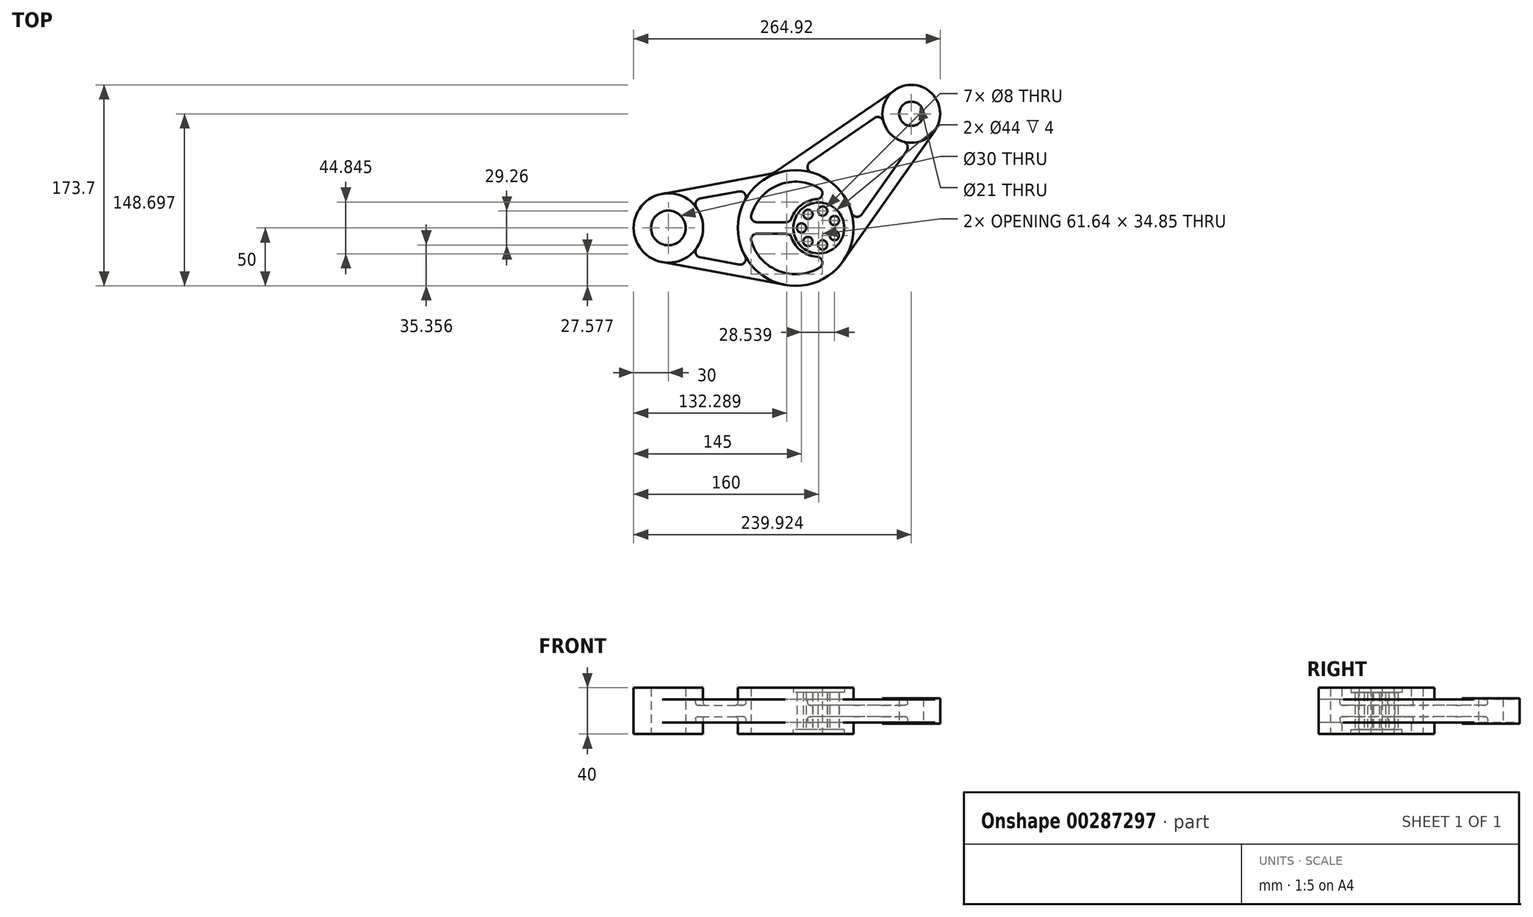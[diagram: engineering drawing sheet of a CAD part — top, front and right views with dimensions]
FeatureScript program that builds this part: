
annotation { "Feature Type Name" : "Feature", "Feature Type Description" : "" }
export const myFeature = defineFeature(function(context is Context, id is Id, definition is map)
    precondition{}
    {
        {
            var Q0;
            Q0=qCreatedBy(makeId("Top.planeOp"),FACE);
            var sketch = newSketch(context, id + "F0", { "sketchPlane" : qUnion([Q0])});
            skLineSegment(sketch, "E0", {"start": v(0, 0) * mm, "end": v(-130, 0) * mm, "construction": true});
            skLineSegment(sketch, "E1", {"start": v(0, 0) * mm, "end": v(79.92, 98.7) * mm, "construction": true});
            skCircle(sketch, "E2", {"center": v(-130, 0) * mm, "radius": 15 * mm});
            skCircle(sketch, "E3", {"center": v(-130, 0) * mm, "radius": 30 * mm});
            skCircle(sketch, "E4", {"center": v(79.92, 98.7) * mm, "radius": 10.5 * mm});
            skCircle(sketch, "E5", {"center": v(79.92, 98.7) * mm, "radius": 25 * mm});
            skCircle(sketch, "E6", {"center": v(-20, 0) * mm, "radius": 50 * mm});
            skArc(sketch, "E7", {"start": v(-58.33, -11.43) * mm, "mid": v(-34.4, -37.32) * mm, "end": v(0.71, -34.22) * mm});
            skArc(sketch, "E8", {"start": v(-23.57, -8.33) * mm, "mid": v(-15.06, -19.95) * mm, "end": v(-1.56, -24.95) * mm});
            skCircle(sketch, "E9", {"center": v(0, 0) * mm, "radius": 22 * mm});
            skCircle(sketch, "E10", {"center": v(0, 0) * mm, "radius": 15 * mm, "construction": true});
            skCircle(sketch, "E11", {"center": v(-15, 0) * mm, "radius": 4 * mm});
            skCircle(sketch, "E12.1.0", {"center": v(-9.34, 11.74) * mm, "radius": 4 * mm});
            skCircle(sketch, "E12.2.0", {"center": v(3.37, 14.62) * mm, "radius": 4 * mm});
            skCircle(sketch, "E12.3.0", {"center": v(13.54, 6.46) * mm, "radius": 4 * mm});
            skCircle(sketch, "E12.4.0", {"center": v(13.48, -6.58) * mm, "radius": 4 * mm});
            skCircle(sketch, "E12.5.0", {"center": v(3.25, -14.64) * mm, "radius": 4 * mm});
            skCircle(sketch, "E12.6.0", {"center": v(-9.44, -11.66) * mm, "radius": 4 * mm});
            skLineSegment(sketch, "E12.anchor1", {"start": v(0, 0) * mm, "end": v(-15, 0) * mm, "construction": true});
            skLineSegment(sketch, "E12.anchor2", {"start": v(0, 0) * mm, "end": v(-9.44, -11.66) * mm, "construction": true});
            skLineSegment(sketch, "E13", {"start": v(-135.45, -29.5) * mm, "end": v(-29.1, -49.17) * mm});
            skLineSegment(sketch, "E14", {"start": v(-135.45, 29.5) * mm, "end": v(-42, 46.78) * mm});
            skLineSegment(sketch, "E15", {"start": v(65.8, 119.33) * mm, "end": v(-37.4, 48.68) * mm});
            skLineSegment(sketch, "E16", {"start": v(100.38, 84.32) * mm, "end": v(20.9, -28.75) * mm});
            skLineSegment(sketch, "E17", {"start": v(-53.54, -5) * mm, "end": v(-28.28, -5) * mm});
            skLineSegment(sketch, "E18", {"start": v(-53.54, 5) * mm, "end": v(-28.28, 5) * mm});
            skArc(sketch, "E19.trimOffspring", {"start": v(0.71, 34.22) * mm, "mid": v(-34.4, 37.32) * mm, "end": v(-58.33, 11.43) * mm});
            skArc(sketch, "E20.trimOffspring", {"start": v(-1.56, 24.95) * mm, "mid": v(-15.06, 19.95) * mm, "end": v(-23.57, 8.33) * mm});
            skPoint(sketch, "E21.visualSharp", {"position": v(-59.69, 5) * mm});
            skArc(sketch, "E21.filletArc", {"start": v(-58.33, 11.43) * mm, "mid": v(-57.55, 7.01) * mm, "end": v(-53.54, 5) * mm});
            skPoint(sketch, "E22.visualSharp", {"position": v(-59.69, -5) * mm});
            skArc(sketch, "E22.filletArc", {"start": v(-53.54, -5) * mm, "mid": v(-57.55, -7.01) * mm, "end": v(-58.33, -11.43) * mm});
            skPoint(sketch, "E23.visualSharp", {"position": v(-24.5, 5) * mm});
            skArc(sketch, "E23.filletArc", {"start": v(-28.28, 5) * mm, "mid": v(-25.4, 5.92) * mm, "end": v(-23.57, 8.33) * mm});
            skPoint(sketch, "E24.visualSharp", {"position": v(-24.5, -5) * mm});
            skArc(sketch, "E24.filletArc", {"start": v(-23.57, -8.33) * mm, "mid": v(-25.4, -5.92) * mm, "end": v(-28.28, -5) * mm});
            skArc(sketch, "E25", {"start": v(0.71, -34.22) * mm, "mid": v(2.98, -28.75) * mm, "end": v(-1.56, -24.95) * mm});
            skArc(sketch, "E26", {"start": v(-1.56, 24.95) * mm, "mid": v(2.98, 28.75) * mm, "end": v(0.71, 34.22) * mm});
            skArc(sketch, "E27.filletArc", {"start": v(-42, 46.78) * mm, "mid": v(-39.6, 47.49) * mm, "end": v(-37.4, 48.68) * mm});
            skSolve(sketch);
        }
        {
            var Q0;
            Q0=makeQuery(id+"F0.imprint","IMPRINT",FACE,{"disambiguationData":[TD([[makeQuery(id+"F0.imprint","IMPRINT",EDGE,{"derivedFrom":sQuery(id+"F0.wireOp",EDGE,"E2")}),-1.0]])]});
            extrude(context, id + "F1", {"entities" : qUnion([Q0]), "depth" : 20 * mm});
        }
        {
            var Q0;
            Q0=makeQuery(id+"F0.imprint","IMPRINT",FACE,{"disambiguationData":[TD([[makeQuery(id+"F0.imprint","IMPRINT",EDGE,{"derivedFrom":sQuery(id+"F0.wireOp",EDGE,"E7")}),-1.0]])]});
            extrude(context, id + "F2", {"entities" : qUnion([Q0]), "depth" : 20 * mm});
        }
        {
            var Q0;
            Q0=makeQuery(id+"F0.imprint","IMPRINT",FACE,{"disambiguationData":[TD([[makeQuery(id+"F0.imprint","IMPRINT",EDGE,{"derivedFrom":sQuery(id+"F0.wireOp",EDGE,"E9")}),1.0]])]});
            extrude(context, id + "F3", {"entities" : qUnion([Q0]), "operationType" : NewBodyOperationType.ADD, "depth" : 16 * mm});
        }
        {
            var Q0;
            Q0=makeQuery(id+"F0.imprint","IMPRINT",FACE,{"disambiguationData":[TD([[makeQuery(id+"F0.imprint","IMPRINT",EDGE,{"derivedFrom":sQuery(id+"F0.wireOp",EDGE,"E4")}),-1.0]])]});
            extrude(context, id + "F4", {"entities" : qUnion([Q0]), "depth" : 11 * mm});
        }
        {
            var Q0;
            {var subQ0=sQuery(id+"F0.wireOp",EDGE,"E13");Q0=makeQuery(id+"F0.imprint","IMPRINT",FACE,{"disambiguationData":[TD([[makeQuery(id+"F0.imprint","IMPRINT",EDGE,{"derivedFrom":subQ0}),1.0]])]});}
            extrude(context, id + "F5", {"entities" : qUnion([Q0]), "operationType" : NewBodyOperationType.ADD, "depth" : 10 * mm});
        }
        {
            var Q0;
            Q0=makeQuery(id+"F5.opExtrude","CAP_FACE",FACE,{"disambiguationData":[OSD([sQuery(id+"F0.wireOp",EDGE,"E3"),sQuery(id+"F0.wireOp",EDGE,"E5"),sQuery(id+"F0.wireOp",EDGE,"E6"),sQuery(id+"F0.wireOp",EDGE,"E13"),sQuery(id+"F0.wireOp",EDGE,"E14"),sQuery(id+"F0.wireOp",EDGE,"E15"),sQuery(id+"F0.wireOp",EDGE,"E16"),sQuery(id+"F0.wireOp",EDGE,"E27.filletArc")])],"isStart":false});
            var sketch = newSketch(context, id + "F6", { "sketchPlane" : qUnion([Q0])});
            skArc(sketch, "E28.0", {"start": v(-105.68, -17.57) * mm, "mid": v(-100, 0) * mm, "end": v(-105.68, 17.57) * mm});
            skArc(sketch, "E29.0", {"start": v(-63.71, 24.28) * mm, "mid": v(-70, 0) * mm, "end": v(-63.71, -24.28) * mm});
            skLineSegment(sketch, "E30.0", {"start": v(-135.45, 29.5) * mm, "end": v(-42, 46.78) * mm, "construction": true});
            skLineSegment(sketch, "E31.0", {"start": v(-135.45, -29.5) * mm, "end": v(-29.1, -49.17) * mm, "construction": true});
            skLineSegment(sketch, "E32.0", {"start": v(65.8, 119.33) * mm, "end": v(-37.4, 48.68) * mm, "construction": true});
            skLineSegment(sketch, "E33.0", {"start": v(100.38, 84.32) * mm, "end": v(20.9, -28.75) * mm, "construction": true});
            skArc(sketch, "E34.0", {"start": v(55.77, 92.26) * mm, "mid": v(62.14, 81.13) * mm, "end": v(73.19, 74.62) * mm});
            skLineSegment(sketch, "E35.0", {"start": v(-102.54, 25.42) * mm, "end": v(-69, 31.62) * mm});
            skLineSegment(sketch, "E36.0", {"start": v(-102.54, -25.42) * mm, "end": v(-69, -31.62) * mm});
            skLineSegment(sketch, "E37.0", {"start": v(48.11, 95.1) * mm, "end": v(-7.59, 56.97) * mm});
            skLineSegment(sketch, "E38.0", {"start": v(75.93, 66.93) * mm, "end": v(37.12, 11.71) * mm});
            skArc(sketch, "E39.trimOffspring", {"start": v(-135.45, 29.5) * mm, "mid": v(-160, 0) * mm, "end": v(-135.45, -29.5) * mm, "construction": true});
            skArc(sketch, "E40.trimOffspring", {"start": v(28.2, 13.26) * mm, "mid": v(15.57, 35.14) * mm, "end": v(-6.15, 48.04) * mm});
            skArc(sketch, "E41.trimOffspring", {"start": v(-29.1, -49.17) * mm, "mid": v(-1.1, -46.29) * mm, "end": v(20.9, -28.75) * mm, "construction": true});
            skPoint(sketch, "E42.visualSharp", {"position": v(-111.65, 23.73) * mm});
            skArc(sketch, "E42.filletArc", {"start": v(-102.54, 25.42) * mm, "mid": v(-106.27, 22.36) * mm, "end": v(-105.68, 17.57) * mm});
            skPoint(sketch, "E43.visualSharp", {"position": v(-111.65, -23.73) * mm});
            skArc(sketch, "E43.filletArc", {"start": v(-105.68, -17.57) * mm, "mid": v(-106.27, -22.36) * mm, "end": v(-102.54, -25.42) * mm});
            skPoint(sketch, "E44.visualSharp", {"position": v(54.95, 99.78) * mm});
            skArc(sketch, "E44.filletArc", {"start": v(55.77, 92.26) * mm, "mid": v(52.67, 95.66) * mm, "end": v(48.11, 95.1) * mm});
            skPoint(sketch, "E45.visualSharp", {"position": v(80.7, 73.7) * mm});
            skArc(sketch, "E45.filletArc", {"start": v(75.93, 66.93) * mm, "mid": v(76.55, 71.49) * mm, "end": v(73.19, 74.62) * mm});
            skArc(sketch, "E46", {"start": v(-63.71, 24.28) * mm, "mid": v(-64.02, 29.62) * mm, "end": v(-69, 31.62) * mm});
            skArc(sketch, "E47", {"start": v(-69, -31.62) * mm, "mid": v(-64.02, -29.62) * mm, "end": v(-63.71, -24.28) * mm});
            skArc(sketch, "E48", {"start": v(-7.59, 56.97) * mm, "mid": v(-9.7, 52.05) * mm, "end": v(-6.15, 48.04) * mm});
            skArc(sketch, "E49", {"start": v(28.2, 13.26) * mm, "mid": v(32.17, 9.66) * mm, "end": v(37.12, 11.71) * mm});
            skSolve(sketch);
        }
        {
            var Q0;
            Q0=makeQuery(id+"F6.imprint","IMPRINT",FACE,{"disambiguationData":[TD([[makeQuery(id+"F6.imprint","IMPRINT",EDGE,{"derivedFrom":sQuery(id+"F6.wireOp",EDGE,"E28.0")}),-1.0]])]});
            var Q1;
            Q1=makeQuery(id+"F6.imprint","IMPRINT",FACE,{"disambiguationData":[TD([[makeQuery(id+"F6.imprint","IMPRINT",EDGE,{"derivedFrom":sQuery(id+"F6.wireOp",EDGE,"E34.0")}),-1.0]])]});
            extrude(context, id + "F7", {"entities" : qUnion([Q0, Q1]), "operationType" : NewBodyOperationType.REMOVE, "oppositeDirection" : true, "depth" : 5 * mm});
        }
        {
            var Q0;
            Q0=makeQuery(id+"F7.boolean.opBoolean","COPY",EDGE,{"derivedFrom":makeQuery(id+"F7.opExtrude","CAP_EDGE",EDGE,{"disambiguationData":[OSD([sQuery(id+"F6.wireOp",EDGE,"E35.0")])],"isStart":false})});
            var Q1;
            Q1=makeQuery(id+"F7.boolean.opBoolean","COPY",EDGE,{"derivedFrom":makeQuery(id+"F7.opExtrude","CAP_EDGE",EDGE,{"disambiguationData":[OSD([sQuery(id+"F6.wireOp",EDGE,"E28.0")])],"isStart":false})});
            var Q2;
            Q2=makeQuery(id+"F7.boolean.opBoolean","COPY",EDGE,{"derivedFrom":makeQuery(id+"F7.opExtrude","CAP_EDGE",EDGE,{"disambiguationData":[OSD([sQuery(id+"F6.wireOp",EDGE,"E37.0")])],"isStart":false})});
            var Q3;
            Q3=makeQuery(id+"F7.boolean.opBoolean","COPY",EDGE,{"derivedFrom":makeQuery(id+"F7.opExtrude","CAP_EDGE",EDGE,{"disambiguationData":[OSD([sQuery(id+"F6.wireOp",EDGE,"E34.0")])],"isStart":false})});
            var Q4;
            Q4=makeQuery(id+"F7.boolean.opBoolean","COPY",EDGE,{"derivedFrom":makeQuery(id+"F7.opExtrude","CAP_EDGE",EDGE,{"disambiguationData":[OSD([sQuery(id+"F6.wireOp",EDGE,"E38.0")])],"isStart":false})});
            var Q5;
            Q5=makeQuery(id+"F7.boolean.opBoolean","COPY",EDGE,{"derivedFrom":makeQuery(id+"F7.opExtrude","CAP_EDGE",EDGE,{"disambiguationData":[OSD([sQuery(id+"F6.wireOp",EDGE,"29acc3ec-2d48-4ee7-b505-37856d55042b.trimOffspring")])],"isStart":false})});
            var Q6;
            Q6=makeQuery(id+"F7.boolean.opBoolean","COPY",EDGE,{"derivedFrom":makeQuery(id+"F7.opExtrude","CAP_EDGE",EDGE,{"disambiguationData":[OSD([sQuery(id+"F6.wireOp",EDGE,"E29.0")])],"isStart":false})});
            var Q7;
            Q7=makeQuery(id+"F7.boolean.opBoolean","COPY",EDGE,{"derivedFrom":makeQuery(id+"F7.opExtrude","CAP_EDGE",EDGE,{"disambiguationData":[OSD([sQuery(id+"F6.wireOp",EDGE,"E36.0")])],"isStart":false})});
            fillet(context, id + "F8", {"entities" : qUnion([Q0, Q1, Q2, Q3, Q4, Q5, Q6, Q7]), "radius" : 2 * mm, "tangentPropagation" : true, "allowEdgeOverflow" : false});
        }
        {
            var Q0;
            Q0=makeQuery(id+"F1.opExtrude","SWEPT_BODY",BODY,{"disambiguationData":[OSD([sQuery(id+"F0.wireOp",EDGE,"E2"),sQuery(id+"F0.wireOp",EDGE,"E3")])]});
            var Q1;
            Q1=qCreatedBy(makeId("Top.planeOp"),FACE);
            mirror(context, id + "F9", {"operationType" : NewBodyOperationType.ADD, "entities" : qUnion([Q0]), "mirrorPlane" : qUnion([Q1])});
        }
    });
